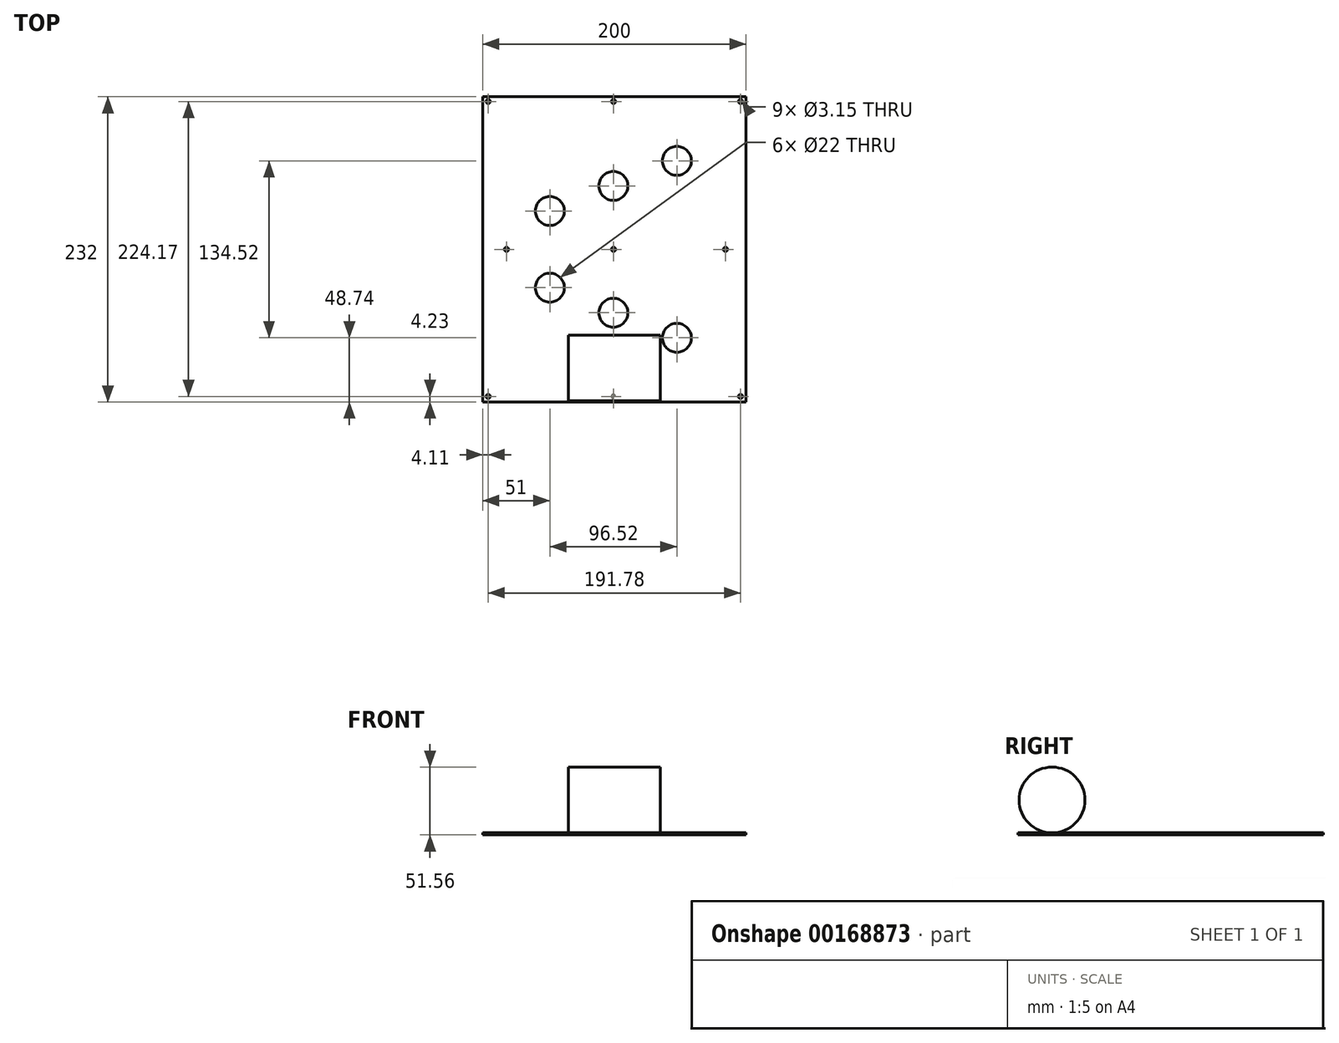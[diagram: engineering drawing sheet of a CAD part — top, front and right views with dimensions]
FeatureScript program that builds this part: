
annotation { "Feature Type Name" : "Feature", "Feature Type Description" : "" }
export const myFeature = defineFeature(function(context is Context, id is Id, definition is map)
    precondition{}
    {
        {
            var Q0;
            Q0=qCreatedBy(makeId("Top.planeOp"),FACE);
            var sketch = newSketch(context, id + "F0", { "sketchPlane" : qUnion([Q0])});
            skLineSegment(sketch, "E0.bottom", {"start": v(100, -116) * mm, "end": v(-100, -116) * mm});
            skLineSegment(sketch, "E0.top", {"start": v(100, 116) * mm, "end": v(-100, 116) * mm});
            skLineSegment(sketch, "E0.left", {"start": v(100, -116) * mm, "end": v(100, 116) * mm});
            skLineSegment(sketch, "E0.right", {"start": v(-100, -116) * mm, "end": v(-100, 116) * mm});
            skPoint(sketch, "E0.middle", {"position": v(0, 0) * mm});
            skLineSegment(sketch, "E1", {"start": v(-49, 138.14) * mm, "end": v(-49, -157.27) * mm, "construction": true});
            skLineSegment(sketch, "E2", {"start": v(-0.74, 141.49) * mm, "end": v(-0.74, -144.34) * mm, "construction": true});
            skLineSegment(sketch, "E3", {"start": v(47.52, 143.4) * mm, "end": v(47.52, -157.27) * mm, "construction": true});
            skLineSegment(sketch, "E4", {"start": v(-203.28, 67.26) * mm, "end": v(180.7, 67.26) * mm, "construction": true});
            skLineSegment(sketch, "E5", {"start": v(-202.8, 48.2) * mm, "end": v(185.48, 48.21) * mm, "construction": true});
            skLineSegment(sketch, "E6", {"start": v(-209.03, 29.16) * mm, "end": v(184.53, 29.16) * mm, "construction": true});
            skLineSegment(sketch, "E7.MirrorCS", {"start": v(-209.03, -29.16) * mm, "end": v(184.53, -29.16) * mm, "construction": true});
            skLineSegment(sketch, "E8.MirrorCS", {"start": v(-202.8, -48.2) * mm, "end": v(185.48, -48.21) * mm, "construction": true});
            skLineSegment(sketch, "E9.MirrorCS", {"start": v(-203.28, -67.26) * mm, "end": v(180.7, -67.26) * mm, "construction": true});
            skCircle(sketch, "E10", {"center": v(-49, 29.16) * mm, "radius": 11 * mm});
            skCircle(sketch, "E11", {"center": v(-0.74, 48.2) * mm, "radius": 11 * mm});
            skCircle(sketch, "E12", {"center": v(-49, -29.16) * mm, "radius": 11 * mm});
            skCircle(sketch, "E13", {"center": v(-0.74, -48.2) * mm, "radius": 11 * mm});
            skCircle(sketch, "E14", {"center": v(47.52, -67.26) * mm, "radius": 11 * mm});
            skCircle(sketch, "E15", {"center": v(47.52, 67.26) * mm, "radius": 11 * mm});
            skPoint(sketch, "E16", {"position": v(47.52, -82.06) * mm});
            skLineSegment(sketch, "E17", {"start": v(-171.66, 112.4) * mm, "end": v(177.1, 112.4) * mm, "construction": true});
            skLineSegment(sketch, "E18", {"start": v(-95.89, -132.6) * mm, "end": v(-95.89, 116) * mm, "construction": true});
            skPoint(sketch, "E19.startSnap0", {"position": v(0, 116) * mm});
            skPoint(sketch, "E20", {"position": v(-95.89, 112.4) * mm});
            skLineSegment(sketch, "E21", {"start": v(-159.47, -111.77) * mm, "end": v(135.44, -111.77) * mm, "construction": true});
            skLineSegment(sketch, "E22", {"start": v(95.89, 123.98) * mm, "end": v(95.89, -126.84) * mm, "construction": true});
            skLineSegment(sketch, "E23", {"start": v(-153.12, 0) * mm, "end": v(127.09, 0) * mm, "construction": true});
            skLineSegment(sketch, "E24", {"start": v(-0.6, 122.31) * mm, "end": v(-0.6, -127.84) * mm, "construction": true});
            skLineSegment(sketch, "E25", {"start": v(-81.95, 122.31) * mm, "end": v(-81.95, -142.2) * mm, "construction": true});
            skLineSegment(sketch, "E26", {"start": v(84.45, 123.65) * mm, "end": v(84.45, -135.19) * mm, "construction": true});
            skPoint(sketch, "E27", {"position": v(-0.6, 112.4) * mm});
            skPoint(sketch, "E28", {"position": v(95.89, 112.4) * mm});
            skPoint(sketch, "E29", {"position": v(-0.6, 29.16) * mm});
            skPoint(sketch, "E30", {"position": v(84.45, 0) * mm});
            skPoint(sketch, "E31", {"position": v(95.89, -111.77) * mm});
            skPoint(sketch, "E32", {"position": v(-0.74, -111.77) * mm});
            skPoint(sketch, "E33", {"position": v(-95.89, -111.77) * mm});
            skPoint(sketch, "E34", {"position": v(-81.95, 0) * mm});
            skPoint(sketch, "E35", {"position": v(-0.6, 0) * mm});
            skSolve(sketch);
        }
        {
            var Q0;
            Q0=makeQuery(id+"F0.imprint","IMPRINT",FACE,{"disambiguationData":[TD([[makeQuery(id+"F0.imprint","IMPRINT",EDGE,{"derivedFrom":sQuery(id+"F0.wireOp",EDGE,"E0.bottom")}),-1.0]])]});
            extrude(context, id + "F1", {"entities" : qUnion([Q0]), "oppositeDirection" : true, "depth" : 1.56 * mm});
        }
        {
            var Q0;
            Q0=sQuery(id+"F0.wireOp",VERTEX,"E20");
            var Q1;
            Q1=makeQuery(id+"F1.opExtrude","SWEPT_BODY",BODY,{"disambiguationData":[OSD([sQuery(id+"F0.wireOp",EDGE,"E0.bottom"),sQuery(id+"F0.wireOp",EDGE,"E0.top"),sQuery(id+"F0.wireOp",EDGE,"E0.left"),sQuery(id+"F0.wireOp",EDGE,"E0.right"),sQuery(id+"F0.wireOp",EDGE,"E10"),sQuery(id+"F0.wireOp",EDGE,"E11"),sQuery(id+"F0.wireOp",EDGE,"E12"),sQuery(id+"F0.wireOp",EDGE,"E13"),sQuery(id+"F0.wireOp",EDGE,"E14"),sQuery(id+"F0.wireOp",EDGE,"E15")])]});
            hole(context, id + "F2", {"style" : HoleStyle.SIMPLE, "endStyle" : HoleEndStyle.THROUGH, "holeDiameter" : 3.15 * mm, "startFromSketch" : true, "locations" : qUnion([Q0]), "scope" : qUnion([Q1]), "isTappedThrough" : true});
        }
        {
            var Q0;
            Q0=sQuery(id+"F0.wireOp",VERTEX,"E27");
            var Q1;
            Q1=sQuery(id+"F0.wireOp",VERTEX,"E28");
            var Q2;
            Q2=sQuery(id+"F0.wireOp",VERTEX,"E30");
            var Q3;
            Q3=sQuery(id+"F0.wireOp",VERTEX,"E34");
            var Q4;
            Q4=sQuery(id+"F0.wireOp",VERTEX,"E35");
            var Q5;
            Q5=sQuery(id+"F0.wireOp",VERTEX,"E32");
            var Q6;
            Q6=sQuery(id+"F0.wireOp",VERTEX,"E33");
            var Q7;
            Q7=sQuery(id+"F0.wireOp",VERTEX,"E31");
            var Q8;
            Q8=makeQuery(id+"F1.opExtrude","SWEPT_BODY",BODY,{"disambiguationData":[OSD([sQuery(id+"F0.wireOp",EDGE,"E0.bottom"),sQuery(id+"F0.wireOp",EDGE,"E0.top"),sQuery(id+"F0.wireOp",EDGE,"E0.left"),sQuery(id+"F0.wireOp",EDGE,"E0.right"),sQuery(id+"F0.wireOp",EDGE,"E10"),sQuery(id+"F0.wireOp",EDGE,"E11"),sQuery(id+"F0.wireOp",EDGE,"E12"),sQuery(id+"F0.wireOp",EDGE,"E13"),sQuery(id+"F0.wireOp",EDGE,"E14"),sQuery(id+"F0.wireOp",EDGE,"E15")])]});
            hole(context, id + "F3", {"style" : HoleStyle.SIMPLE, "endStyle" : HoleEndStyle.THROUGH, "holeDiameter" : 3.15 * mm, "startFromSketch" : true, "locations" : qUnion([Q0, Q1, Q2, Q3, Q4, Q5, Q6, Q7]), "scope" : qUnion([Q8]), "isTappedThrough" : true});
        }
        {
            var Q0;
            Q0=qCreatedBy(makeId("Right.planeOp"),FACE);
            var sketch = newSketch(context, id + "F4", { "sketchPlane" : qUnion([Q0])});
            skCircle(sketch, "E36", {"center": v(-90.18, 25) * mm, "radius": 25 * mm});
            skSolve(sketch);
        }
        {
            var Q0;
            Q0=makeQuery(id+"F4.imprint","IMPRINT",FACE,{"disambiguationData":[TD([[makeQuery(id+"F4.imprint","IMPRINT",EDGE,{"derivedFrom":sQuery(id+"F4.wireOp",EDGE,"E36")}),1.0]])]});
            var Q1;
            Q1=sQuery(id+"F4.wireOp",EDGE,"E36");
            extrude(context, id + "F5", {"entities" : qUnion([Q0]), "surfaceEntities" : qUnion([Q1]), "endBound" : BoundingType.SYMMETRIC, "depth" : 70 * mm, "offsetDistance" : 25 * mm});
        }
    });
